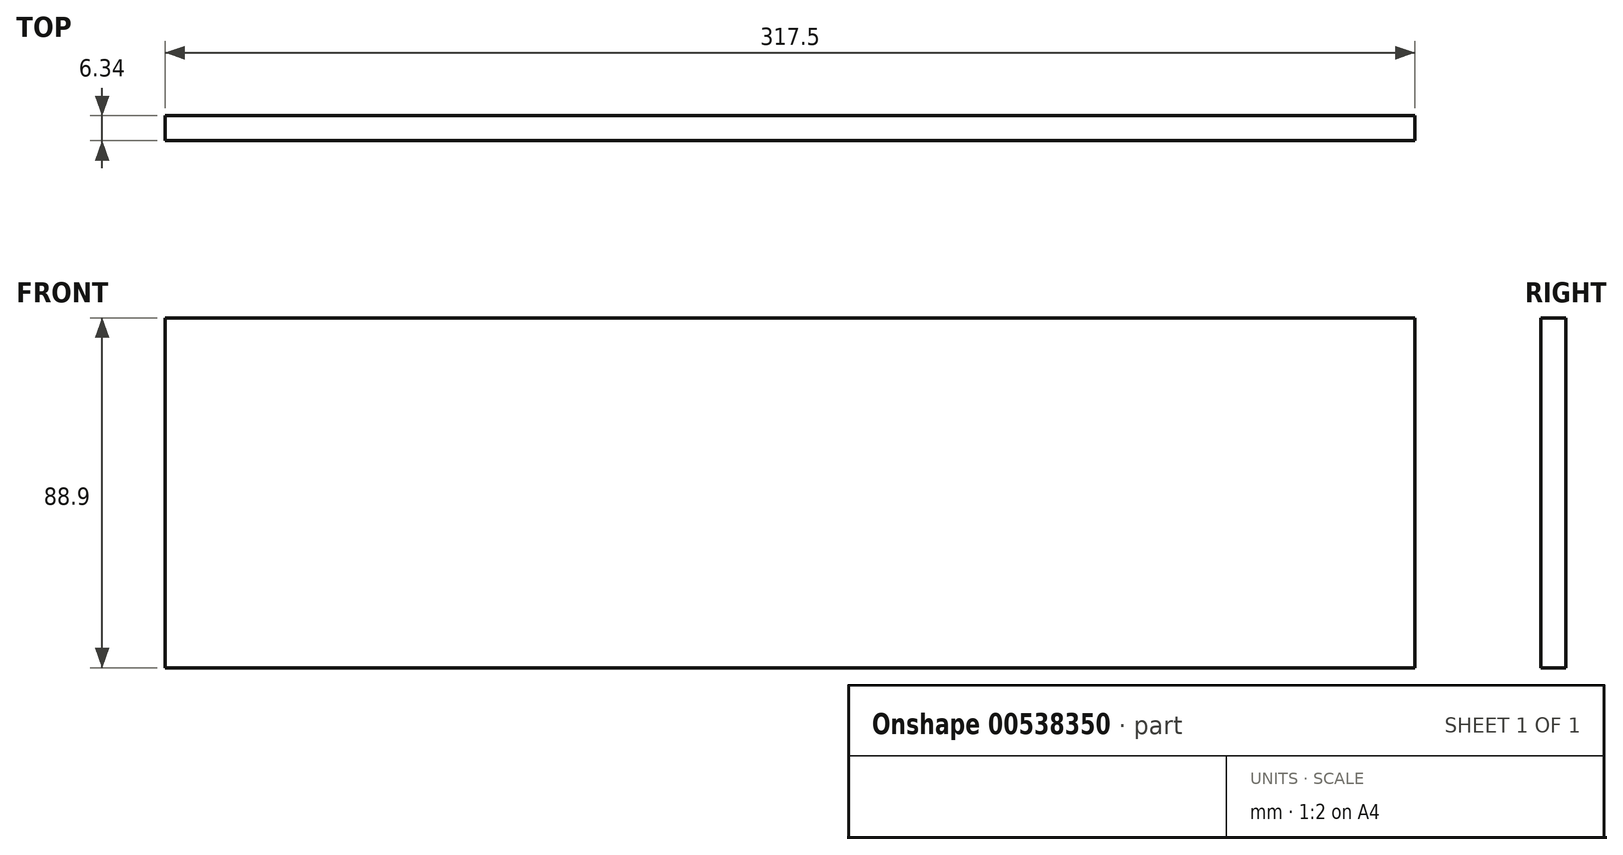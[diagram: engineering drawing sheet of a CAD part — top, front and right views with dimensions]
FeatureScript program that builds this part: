
annotation { "Feature Type Name" : "Feature", "Feature Type Description" : "" }
export const myFeature = defineFeature(function(context is Context, id is Id, definition is map)
    precondition{}
    {
        {
            var Q0;
            Q0=qCreatedBy(makeId("Front.planeOp"),FACE);
            var sketch = newSketch(context, id + "F0", { "sketchPlane" : qUnion([Q0])});
            skLineSegment(sketch, "E0.bottom", {"start": v(158.75, 44.45) * mm, "end": v(-158.75, 44.45) * mm});
            skLineSegment(sketch, "E0.top", {"start": v(158.75, -44.45) * mm, "end": v(-158.75, -44.45) * mm});
            skLineSegment(sketch, "E0.left", {"start": v(158.75, 44.45) * mm, "end": v(158.75, -44.45) * mm});
            skLineSegment(sketch, "E0.right", {"start": v(-158.75, 44.45) * mm, "end": v(-158.75, -44.45) * mm});
            skPoint(sketch, "E0.middle", {"position": v(0, 0) * mm});
            skSolve(sketch);
        }
        {
            var Q0;
            Q0=makeQuery(id+"F0.imprint","IMPRINT",FACE,{"disambiguationData":[TD([[makeQuery(id+"F0.imprint","IMPRINT",EDGE,{"derivedFrom":sQuery(id+"F0.wireOp",EDGE,"E0.bottom")}),1.0]])]});
            extrude(context, id + "F1", {"entities" : qUnion([Q0]), "endBound" : BoundingType.SYMMETRIC, "depth" : 6.35 * mm, "offsetDistance" : 25.4 * mm});
        }
    });
